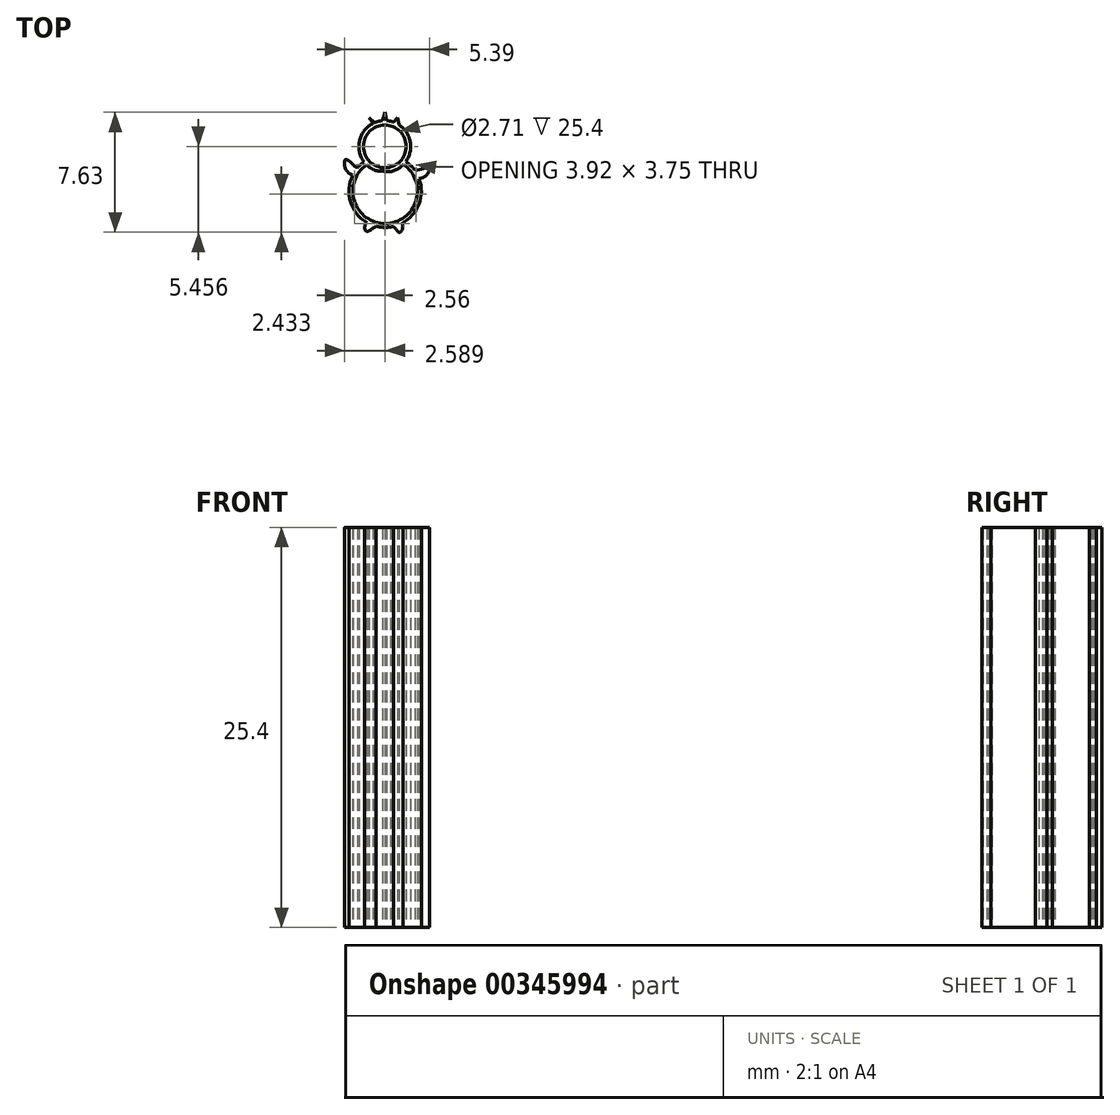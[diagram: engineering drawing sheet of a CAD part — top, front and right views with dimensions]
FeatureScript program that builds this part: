
annotation { "Feature Type Name" : "Feature", "Feature Type Description" : "" }
export const myFeature = defineFeature(function(context is Context, id is Id, definition is map)
    precondition{}
    {
        {
            var Q0;
            Q0=qCreatedBy(makeId("Top.planeOp"),FACE);
            var sketch = newSketch(context, id + "F0", { "sketchPlane" : qUnion([Q0])});
            skCircle(sketch, "E0", {"center": v(34.5, 23.26) * mm, "radius": 1.36 * mm});
            skArc(sketch, "E1", {"start": v(35.04, 24.8) * mm, "mid": v(33.76, 21.78) * mm, "end": v(35.4, 24.63) * mm});
            skArc(sketch, "E2", {"start": v(33.33, 22.09) * mm, "mid": v(34.53, 18.36) * mm, "end": v(35.67, 22.1) * mm});
            skArc(sketch, "E3", {"start": v(33.17, 22.28) * mm, "mid": v(32.96, 22.1) * mm, "end": v(32.77, 21.9) * mm});
            skArc(sketch, "E4.MirrorC", {"start": v(35.4, 24.63) * mm, "mid": v(33.9, 21.72) * mm, "end": v(34.74, 24.88) * mm});
            skPoint(sketch, "E5.MirrorCS.end.orphan", {"position": v(33.24, 24.32) * mm});
            skPoint(sketch, "E5.MirrorCS.start.orphan", {"position": v(33.48, 25.4) * mm});
            skPoint(sketch, "E6.MirrorCS.end.orphan", {"position": v(33.48, 24.55) * mm});
            skPoint(sketch, "E7.MirrorCS.end.orphan", {"position": v(33.76, 25.43) * mm});
            skPoint(sketch, "E8.MirrorCS.end.orphan", {"position": v(33.76, 24.73) * mm});
            skPoint(sketch, "E9.MirrorCS.end.orphan", {"position": v(34.03, 25.43) * mm});
            skPoint(sketch, "E10.MirrorCS.start.orphan", {"position": v(34.49, 25.43) * mm});
            skPoint(sketch, "E11.end.orphan", {"position": v(35.75, 24.32) * mm});
            skPoint(sketch, "E12.MirrorCS.start.orphan", {"position": v(34.24, 24.88) * mm});
            skPoint(sketch, "E13.end.orphan", {"position": v(35.5, 25.4) * mm});
            skPoint(sketch, "E14.MirrorCS.end.orphan", {"position": v(34.03, 24.88) * mm});
            skPoint(sketch, "E14.MirrorCS.start.orphan", {"position": v(34.24, 25.4) * mm});
            skPoint(sketch, "E15.start.orphan", {"position": v(34.74, 24.88) * mm});
            skPoint(sketch, "E16.start.orphan", {"position": v(34.74, 25.4) * mm});
            skPoint(sketch, "E17.start.orphan", {"position": v(35.22, 25.43) * mm});
            skPoint(sketch, "E18.end.orphan", {"position": v(34.95, 25.43) * mm});
            skPoint(sketch, "E18.start.orphan", {"position": v(34.95, 24.88) * mm});
            skPoint(sketch, "E19.end.orphan", {"position": v(34.5, 25.43) * mm});
            skPoint(sketch, "E19.start.orphan", {"position": v(34.5, 24.9) * mm});
            skLineSegment(sketch, "E20", {"start": v(33.76, 24.73) * mm, "end": v(33.48, 25.08) * mm});
            skLineSegment(sketch, "E21", {"start": v(33.48, 25.08) * mm, "end": v(33.83, 24.76) * mm});
            skLineSegment(sketch, "E22", {"start": v(34.5, 25.43) * mm, "end": v(34.6, 24.9) * mm});
            skLineSegment(sketch, "E23", {"start": v(34.6, 24.9) * mm, "end": v(34.49, 25.43) * mm});
            skLineSegment(sketch, "E24", {"start": v(34.5, 25.43) * mm, "end": v(34.35, 24.9) * mm});
            skPoint(sketch, "E25.MirrorP", {"position": v(35.5, 24.55) * mm});
            skPoint(sketch, "E26.MirrorP", {"position": v(35.22, 24.73) * mm});
            skPoint(sketch, "E27.orphan", {"position": v(34.51, 12.5) * mm});
            skEllipse(sketch, "E28", {"center": v(34.48, 23.03) * mm, "majorRadius": 0.26 * mm, "minorRadius": 0.12 * mm, "majorAxis": v(1, 0)});
            skLineSegment(sketch, "E29", {"start": v(34.22, 23.03) * mm, "end": v(34.74, 23.03) * mm});
            skCircle(sketch, "E30", {"center": v(35.07, 23.35) * mm, "radius": 0.1 * mm});
            skCircle(sketch, "E31", {"center": v(33.94, 23.35) * mm, "radius": 0.1 * mm});
            skCircle(sketch, "E32", {"center": v(33.94, 23.35) * mm, "radius": 0.14 * mm});
            skCircle(sketch, "E33", {"center": v(35.07, 23.35) * mm, "radius": 0.12 * mm});
            skFitSpline(sketch, "E34", {"points": [v(32.77, 21.9) * mm, v(32.37, 22.2) * mm, v(32, 22.43) * mm, v(31.94, 22.04) * mm, v(32.45, 21.43) * mm, v(36.67, 21.2) * mm, v(37.3, 21.65) * mm, v(37.3, 21.9) * mm, v(36.4, 21.73) * mm, v(32.77, 21.9) * mm]});
            skFitSpline(sketch, "E35", {"points": [v(33.35, 18.43) * mm, v(33.32, 17.87) * mm, v(33.95, 18.18) * mm, v(35.03, 18.17) * mm, v(35.43, 17.8) * mm, v(35.57, 18.37) * mm, v(33.35, 18.43) * mm]});
            skArc(sketch, "E36", {"start": v(33.62, 21.86) * mm, "mid": v(34.53, 18.71) * mm, "end": v(35.38, 21.87) * mm});
            skArc(sketch, "E37", {"start": v(33.77, 21.78) * mm, "mid": v(34.53, 18.86) * mm, "end": v(35.23, 21.79) * mm});
            skLineSegment(sketch, "E38", {"start": v(35.15, 24.76) * mm, "end": v(35.15, 24.76) * mm});
            skLineSegment(sketch, "E39", {"start": v(35.29, 25.08) * mm, "end": v(35.4, 24.63) * mm});
            skLineSegment(sketch, "E40", {"start": v(35.29, 25.08) * mm, "end": v(35.04, 24.8) * mm});
            skArc(sketch, "E41.trimOffspring", {"start": v(32.45, 21.43) * mm, "mid": v(32.31, 19.75) * mm, "end": v(33.35, 18.43) * mm});
            skArc(sketch, "E42.trimOffspring", {"start": v(36.4, 21.73) * mm, "mid": v(36.14, 22.04) * mm, "end": v(35.83, 22.3) * mm});
            skArc(sketch, "E43.trimOffspring", {"start": v(35.57, 18.37) * mm, "mid": v(36.66, 19.58) * mm, "end": v(36.67, 21.2) * mm});
            skArc(sketch, "E44.trimOffspring", {"start": v(33.95, 18.18) * mm, "mid": v(34.49, 18.11) * mm, "end": v(35.03, 18.17) * mm});
            skSolve(sketch);
        }
        {
            var Q0;
            Q0 = qSketchRegion(id + "F0", true);
            var Q1;
            {var subQ11=sQuery(id+"F0.wireOp",EDGE,"E1");Q1=makeQuery(id+"F0.imprint","IMPRINT",FACE,{"disambiguationData":[TD([[makeQuery(id+"F0.imprint","IMPRINT",EDGE,{"derivedFrom":subQ11}),1.0]])]});}
            extrude(context, id + "F1", {"entities" : qUnion([Q0, Q1]), "depth" : 25.4 * mm});
        }
    });
